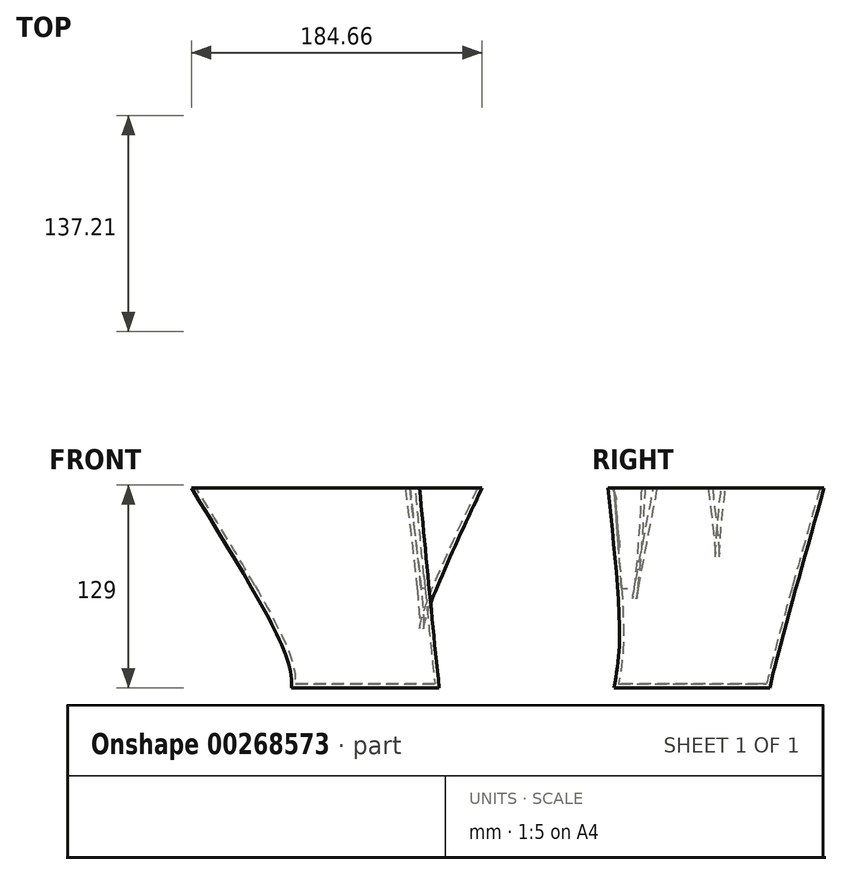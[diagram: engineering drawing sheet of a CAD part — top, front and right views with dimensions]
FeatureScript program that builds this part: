
annotation { "Feature Type Name" : "Feature", "Feature Type Description" : "" }
export const myFeature = defineFeature(function(context is Context, id is Id, definition is map)
    precondition{}
    {
        {
            var Q0;
            Q0=qCreatedBy(makeId("Top.planeOp"),FACE);
            cPlane(context, id + "F0", {"entities" : qUnion([Q0]), "cplaneType" : CPlaneType.OFFSET, "offset" : 127 * mm, "width" : 152.4 * mm, "height" : 152.4 * mm});
        }
        {
            var Q0;
            Q0=qCreatedBy(id+"F0.planeOp",FACE);
            var sketch = newSketch(context, id + "F1", { "sketchPlane" : qUnion([Q0])});
            skFitSpline(sketch, "E0", {"points": [v(-34.36, 15.63) * mm, v(-107.71, 19.04) * mm, v(-84.5, -29.25) * mm, v(-21.05, -25.23) * mm, v(33.43, -52.77) * mm, v(30.95, 11.3) * mm, v(73.97, 56.49) * mm, v(-5.88, 79.7) * mm, v(-34.36, 15.63) * mm]});
            skSolve(sketch);
        }
        {
            var Q0;
            Q0=qCreatedBy(makeId("Top.planeOp"),FACE);
            var sketch = newSketch(context, id + "F2", { "sketchPlane" : qUnion([Q0])});
            skEllipse(sketch, "E1", {"center": v(0, 0) * mm, "majorRadius": 61.09 * mm, "minorRadius": 30.25 * mm, "majorAxis": v(-0.68, 0.74)});
            skSolve(sketch);
        }
        {
            var Q0;
            Q0=makeQuery(id+"F2.imprint","IMPRINT",FACE,{"disambiguationData":[TD([[makeQuery(id+"F2.imprint","IMPRINT",EDGE,{"derivedFrom":sQuery(id+"F2.wireOp",EDGE,"E1")}),1.0]])]});
            var Q1;
            Q1=makeQuery(id+"F1.imprint","IMPRINT",FACE,{"disambiguationData":[TD([[makeQuery(id+"F1.imprint","IMPRINT",EDGE,{"derivedFrom":sQuery(id+"F1.wireOp",EDGE,"E0")}),1.0]])]});
            loft(context, id + "F3", {"sheetProfilesArray" : [{ "sheetProfileEntities" : qUnion([Q0]) }, { "sheetProfileEntities" : qUnion([Q1]) }]});
        }
        {
            var Q0;
            Q0=makeQuery(id+"F3.opLoft","CAP_FACE",FACE,{"disambiguationData":[OSD([makeQuery(id+"F1.imprint","IMPRINT",FACE,{"disambiguationData":[TD([[makeQuery(id+"F1.imprint","IMPRINT",EDGE,{"derivedFrom":sQuery(id+"F1.wireOp",EDGE,"E0")}),1.0]])]})])],"isStart":true});
            shell(context, id + "F4", {"entities" : qUnion([Q0]), "thickness" : 2.54 * mm});
        }
    });
